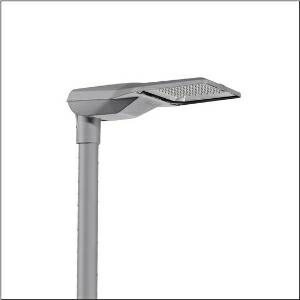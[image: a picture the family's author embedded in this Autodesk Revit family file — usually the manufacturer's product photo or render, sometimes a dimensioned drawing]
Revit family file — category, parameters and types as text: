
# Revit family: streetlight_sl_21_iq_midi___st1_0a_5xe3d41d08nb_8ddf
name_source: partatom
category: Lighting Fixtures
units: mm (PartAtom-declared; Revit-internal decimal feet)

## family parameters
Cut with Voids When Loaded = No
Host = Face
Light Source = No
Part Type = Normal
Room Calculation Point = No
Round Connector Dimension = Use Diameter
Shared = No

## types (1)
- --- (1 x LED, 24250 lm, 155.5 W, 4000K)
    Apparent Load = 155 VA
    CIE Flux Codes = 40 73 97 100 100
    Color Rendering = 70
    Color Temperature = 4000K
    Default Elevation = 1800 mm
    Description = Streetlight SL 21 iQ midi, mast luminaire, primary light control with lens, of PMMA, primary optical cover: cover, of toughened safety glass, transparent, light distribution: ST1.0a, light emission: direct distribution, primary light characteristic: asymmetric, installation type: post-top, side-entry, LED, High Power LED, rated luminous flux: 24.250lm, luminous efficacy: 156lm/W, light colour: 740, colour temperature: 4000K, control gear: iQ-Comfort, control: Auto-Match, Temp-Guard, Lumen-Switch, Night-Set, Smart-Wire, Light-Fading, Desk-Remote (wireless, voltage-free reading and setting of iQ features in the workshop via application-optimized NFC function/RFID function), optimised constant luminous flux control (CLO 2.0), pre-setting: linear dimming characteristic, mains connection: 230..240V, AC, 50/60Hz, start of lifetime: 156W, end of service life: 162W, reduction: 69W, luminaire housing, of diecast aluminium, powder-coated, Siteco® metallic grey (DB 702S), corrosivity category C5 mid according to DIN EN ISO 12944, please order mast flange separately, inclination adjustable: 0°, 5°, 10°, 15°, sealing non-destructively replaceable, multi-level sealing system, length: 644mm, width: 335mm, height: 110mm, mast flange for spigot size: 42mm (side-entry): 5XC10008XM4, 60/48mm (side-entry/post-top): 5XC10108XM2, 76/60mm (side-entry/post-top): 5XC10108XM1, mounting height: 4..8m, protection rating (complete): IP66, insulation class (complete): insulation class II (safety insulation), certification: CE, ENEC, ENEC+, VDE, impact resistance: IK10, permissible operating ambient temperature for outdoor applications: -40..+50°C, standard-compliant lighting for roads and squares, packaging unit: 1 piece

Light Distribution: ST1.0a
    Height = 111 mm
    Lamp = 1 x LED
    Lamp Light Flux = 24250 lm
    Lamp Power = 155.5 W
    Lamp count = 1
    Length = 644 mm
    Luminous efficacy = 156 lm/W
    Manufacturer = Siteco
    ModVariant = No
    Model = 5XE3D41D08NB
    Number of Poles = 1
    OnlyDefault = Yes
    Power Factor = 1
    Product Name = Streetlight SL 21 iQ midi | ST1.0a
    Product group = mast luminaire | pylon top
    ProductGroupID = 6100
    Protection Class = Protection class II
    Protection Degree = IP 66
    RLX_Detail_Level = 1
    RLX_Emergency_Light_Flux = 0 lm
    RLX_Emergency_Type = 0
    RLX_Emergency_Type_DB = No
    RlxData = <blob elided: 27193 chars, md5=ad514cca>
    Socket = socket
    Standby Power = 0 W
    System Light Flux = 24250 lm
    System Power = 155 W
    Type Comments = factory setting: luminous flux: 100 % | dim-lin: 254 | 823 mA
    Type Image = l_1004298.jpg
    URL = http://relux.com
    VarID = @adj_170810
    Voltage = 0 V
    Weight = 0.00 kg
    Width = 336 mm

## geometry (parser evidence)
native form markers: Blend x4, Sweep x10
no freeform markers — native parametric forms only
